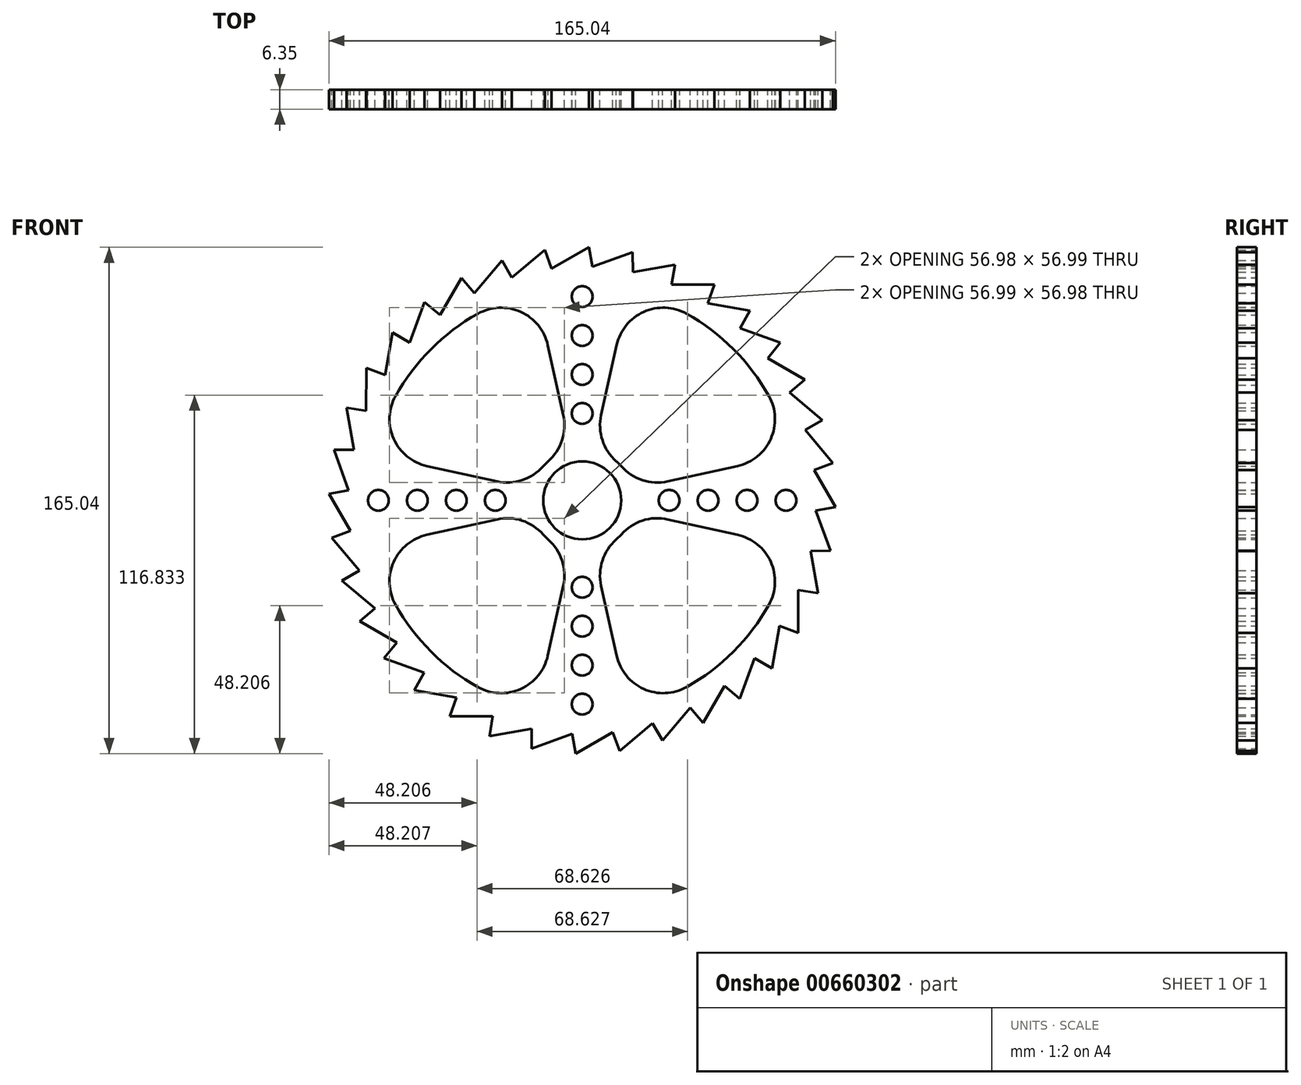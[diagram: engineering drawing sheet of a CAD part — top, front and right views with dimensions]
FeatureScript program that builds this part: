
annotation { "Feature Type Name" : "Feature", "Feature Type Description" : "" }
export const myFeature = defineFeature(function(context is Context, id is Id, definition is map)
    precondition{}
    {
        {
            var Q0;
            Q0=qCreatedBy(makeId("Front.planeOp"),FACE);
            var sketch = newSketch(context, id + "F0", { "sketchPlane" : qUnion([Q0])});
            skCircle(sketch, "E0", {"center": v(0, 0) * mm, "radius": 82.55 * mm, "construction": true});
            skCircle(sketch, "E1", {"center": v(0, 0) * mm, "radius": 76.2 * mm, "construction": true});
            skLineSegment(sketch, "E2", {"start": v(0, 0) * mm, "end": v(-97.62, 21.64) * mm, "construction": true});
            skLineSegment(sketch, "E3", {"start": v(0, 0) * mm, "end": v(-99.58, 4.35) * mm, "construction": true});
            skLineSegment(sketch, "E4", {"start": v(-76.13, 3.32) * mm, "end": v(-80.9, 16.46) * mm});
            skLineSegment(sketch, "E5", {"start": v(-80.9, 16.46) * mm, "end": v(-74.4, 16.5) * mm});
            skLineSegment(sketch, "E6.1.0", {"start": v(-82.52, 2.16) * mm, "end": v(-76.13, 3.32) * mm});
            skLineSegment(sketch, "E6.1.1", {"start": v(-75.55, -9.95) * mm, "end": v(-82.52, 2.16) * mm});
            skLineSegment(sketch, "E6.2.0", {"start": v(-81.64, -12.2) * mm, "end": v(-75.55, -9.95) * mm});
            skLineSegment(sketch, "E6.2.1", {"start": v(-72.67, -22.91) * mm, "end": v(-81.64, -12.2) * mm});
            skLineSegment(sketch, "E6.3.0", {"start": v(-78.28, -26.2) * mm, "end": v(-72.67, -22.91) * mm});
            skLineSegment(sketch, "E6.3.1", {"start": v(-67.6, -35.19) * mm, "end": v(-78.28, -26.2) * mm});
            skLineSegment(sketch, "E6.4.0", {"start": v(-72.55, -39.4) * mm, "end": v(-67.6, -35.19) * mm});
            skLineSegment(sketch, "E6.4.1", {"start": v(-60.45, -46.39) * mm, "end": v(-72.55, -39.4) * mm});
            skLineSegment(sketch, "E6.5.0", {"start": v(-64.6, -51.4) * mm, "end": v(-60.45, -46.39) * mm});
            skLineSegment(sketch, "E6.5.1", {"start": v(-51.48, -56.18) * mm, "end": v(-64.6, -51.4) * mm});
            skLineSegment(sketch, "E6.6.0", {"start": v(-54.7, -61.83) * mm, "end": v(-51.48, -56.18) * mm});
            skLineSegment(sketch, "E6.6.1", {"start": v(-40.94, -64.27) * mm, "end": v(-54.7, -61.83) * mm});
            skLineSegment(sketch, "E6.7.0", {"start": v(-43.13, -70.39) * mm, "end": v(-40.94, -64.27) * mm});
            skLineSegment(sketch, "E6.7.1", {"start": v(-29.16, -70.4) * mm, "end": v(-43.13, -70.39) * mm});
            skLineSegment(sketch, "E6.8.0", {"start": v(-30.25, -76.8) * mm, "end": v(-29.16, -70.4) * mm});
            skLineSegment(sketch, "E6.8.1", {"start": v(-16.5, -74.4) * mm, "end": v(-30.25, -76.8) * mm});
            skLineSegment(sketch, "E6.9.0", {"start": v(-16.46, -80.9) * mm, "end": v(-16.5, -74.4) * mm});
            skLineSegment(sketch, "E6.9.1", {"start": v(-3.32, -76.13) * mm, "end": v(-16.46, -80.9) * mm});
            skLineSegment(sketch, "E6.10.0", {"start": v(-2.16, -82.52) * mm, "end": v(-3.32, -76.13) * mm});
            skLineSegment(sketch, "E6.10.1", {"start": v(9.95, -75.55) * mm, "end": v(-2.16, -82.52) * mm});
            skLineSegment(sketch, "E6.11.0", {"start": v(12.2, -81.64) * mm, "end": v(9.95, -75.55) * mm});
            skLineSegment(sketch, "E6.11.1", {"start": v(22.91, -72.67) * mm, "end": v(12.2, -81.64) * mm});
            skLineSegment(sketch, "E6.12.0", {"start": v(26.2, -78.28) * mm, "end": v(22.91, -72.67) * mm});
            skLineSegment(sketch, "E6.12.1", {"start": v(35.19, -67.6) * mm, "end": v(26.2, -78.28) * mm});
            skLineSegment(sketch, "E6.13.0", {"start": v(39.4, -72.55) * mm, "end": v(35.19, -67.6) * mm});
            skLineSegment(sketch, "E6.13.1", {"start": v(46.39, -60.45) * mm, "end": v(39.4, -72.55) * mm});
            skLineSegment(sketch, "E6.14.0", {"start": v(51.4, -64.6) * mm, "end": v(46.39, -60.45) * mm});
            skLineSegment(sketch, "E6.14.1", {"start": v(56.18, -51.48) * mm, "end": v(51.4, -64.6) * mm});
            skLineSegment(sketch, "E6.15.0", {"start": v(61.83, -54.7) * mm, "end": v(56.18, -51.48) * mm});
            skLineSegment(sketch, "E6.15.1", {"start": v(64.27, -40.94) * mm, "end": v(61.83, -54.7) * mm});
            skLineSegment(sketch, "E6.16.0", {"start": v(70.39, -43.13) * mm, "end": v(64.27, -40.94) * mm});
            skLineSegment(sketch, "E6.16.1", {"start": v(70.4, -29.16) * mm, "end": v(70.39, -43.13) * mm});
            skLineSegment(sketch, "E6.17.0", {"start": v(76.8, -30.25) * mm, "end": v(70.4, -29.16) * mm});
            skLineSegment(sketch, "E6.17.1", {"start": v(74.4, -16.5) * mm, "end": v(76.8, -30.25) * mm});
            skLineSegment(sketch, "E6.18.0", {"start": v(80.9, -16.46) * mm, "end": v(74.4, -16.5) * mm});
            skLineSegment(sketch, "E6.18.1", {"start": v(76.13, -3.32) * mm, "end": v(80.9, -16.46) * mm});
            skLineSegment(sketch, "E6.19.0", {"start": v(82.52, -2.16) * mm, "end": v(76.13, -3.32) * mm});
            skLineSegment(sketch, "E6.19.1", {"start": v(75.55, 9.95) * mm, "end": v(82.52, -2.16) * mm});
            skLineSegment(sketch, "E6.20.0", {"start": v(81.64, 12.2) * mm, "end": v(75.55, 9.95) * mm});
            skLineSegment(sketch, "E6.20.1", {"start": v(72.67, 22.91) * mm, "end": v(81.64, 12.2) * mm});
            skLineSegment(sketch, "E6.21.0", {"start": v(78.28, 26.2) * mm, "end": v(72.67, 22.91) * mm});
            skLineSegment(sketch, "E6.21.1", {"start": v(67.6, 35.19) * mm, "end": v(78.28, 26.2) * mm});
            skLineSegment(sketch, "E6.22.0", {"start": v(72.55, 39.4) * mm, "end": v(67.6, 35.19) * mm});
            skLineSegment(sketch, "E6.22.1", {"start": v(60.45, 46.39) * mm, "end": v(72.55, 39.4) * mm});
            skLineSegment(sketch, "E6.23.0", {"start": v(64.6, 51.4) * mm, "end": v(60.45, 46.39) * mm});
            skLineSegment(sketch, "E6.23.1", {"start": v(51.48, 56.18) * mm, "end": v(64.6, 51.4) * mm});
            skLineSegment(sketch, "E6.24.0", {"start": v(54.7, 61.83) * mm, "end": v(51.48, 56.18) * mm});
            skLineSegment(sketch, "E6.24.1", {"start": v(40.94, 64.27) * mm, "end": v(54.7, 61.83) * mm});
            skLineSegment(sketch, "E6.25.0", {"start": v(43.13, 70.39) * mm, "end": v(40.94, 64.27) * mm});
            skLineSegment(sketch, "E6.25.1", {"start": v(29.16, 70.4) * mm, "end": v(43.13, 70.39) * mm});
            skLineSegment(sketch, "E6.26.0", {"start": v(30.25, 76.8) * mm, "end": v(29.16, 70.4) * mm});
            skLineSegment(sketch, "E6.26.1", {"start": v(16.5, 74.4) * mm, "end": v(30.25, 76.8) * mm});
            skLineSegment(sketch, "E6.27.0", {"start": v(16.46, 80.9) * mm, "end": v(16.5, 74.4) * mm});
            skLineSegment(sketch, "E6.27.1", {"start": v(3.32, 76.13) * mm, "end": v(16.46, 80.9) * mm});
            skLineSegment(sketch, "E6.28.0", {"start": v(2.16, 82.52) * mm, "end": v(3.32, 76.13) * mm});
            skLineSegment(sketch, "E6.28.1", {"start": v(-9.95, 75.55) * mm, "end": v(2.16, 82.52) * mm});
            skLineSegment(sketch, "E6.29.0", {"start": v(-12.2, 81.64) * mm, "end": v(-9.95, 75.55) * mm});
            skLineSegment(sketch, "E6.29.1", {"start": v(-22.91, 72.67) * mm, "end": v(-12.2, 81.64) * mm});
            skLineSegment(sketch, "E6.30.0", {"start": v(-26.2, 78.28) * mm, "end": v(-22.91, 72.67) * mm});
            skLineSegment(sketch, "E6.30.1", {"start": v(-35.19, 67.6) * mm, "end": v(-26.2, 78.28) * mm});
            skLineSegment(sketch, "E6.31.0", {"start": v(-39.4, 72.55) * mm, "end": v(-35.19, 67.6) * mm});
            skLineSegment(sketch, "E6.31.1", {"start": v(-46.39, 60.45) * mm, "end": v(-39.4, 72.55) * mm});
            skLineSegment(sketch, "E6.32.0", {"start": v(-51.4, 64.6) * mm, "end": v(-46.39, 60.45) * mm});
            skLineSegment(sketch, "E6.32.1", {"start": v(-56.18, 51.48) * mm, "end": v(-51.4, 64.6) * mm});
            skLineSegment(sketch, "E6.33.0", {"start": v(-61.83, 54.7) * mm, "end": v(-56.18, 51.48) * mm});
            skLineSegment(sketch, "E6.33.1", {"start": v(-64.27, 40.94) * mm, "end": v(-61.83, 54.7) * mm});
            skLineSegment(sketch, "E6.34.0", {"start": v(-70.39, 43.13) * mm, "end": v(-64.27, 40.94) * mm});
            skLineSegment(sketch, "E6.34.1", {"start": v(-70.4, 29.16) * mm, "end": v(-70.39, 43.13) * mm});
            skLineSegment(sketch, "E6.35.0", {"start": v(-76.8, 30.25) * mm, "end": v(-70.4, 29.16) * mm});
            skLineSegment(sketch, "E6.35.1", {"start": v(-74.4, 16.5) * mm, "end": v(-76.8, 30.25) * mm});
            skCircle(sketch, "E7", {"center": v(0, 0) * mm, "radius": 16.92 * mm, "construction": true});
            skLineSegment(sketch, "E8", {"start": v(0, 0) * mm, "end": v(97.72, 0) * mm, "construction": true});
            skLineSegment(sketch, "E9", {"start": v(27.83, 6.17) * mm, "end": v(50.62, 11.22) * mm});
            skLineSegment(sketch, "E10", {"start": v(0, 0) * mm, "end": v(0, 86.25) * mm, "construction": true});
            skArc(sketch, "E11", {"start": v(34.02, 60.84) * mm, "mid": v(49.3, 49.3) * mm, "end": v(60.84, 34.02) * mm});
            skLineSegment(sketch, "E12", {"start": v(6.17, 27.83) * mm, "end": v(11.22, 50.62) * mm});
            skPoint(sketch, "E13.visualSharp", {"position": v(15.09, 68.06) * mm});
            skArc(sketch, "E13.filletArc", {"start": v(34.02, 60.84) * mm, "mid": v(20.06, 61.46) * mm, "end": v(11.22, 50.62) * mm});
            skPoint(sketch, "E14.visualSharp", {"position": v(68.06, 15.09) * mm});
            skArc(sketch, "E14.filletArc", {"start": v(50.62, 11.22) * mm, "mid": v(61.46, 20.06) * mm, "end": v(60.84, 34.02) * mm});
            skArc(sketch, "E15", {"start": v(11.13, 12.74) * mm, "mid": v(11.96, 11.96) * mm, "end": v(12.74, 11.13) * mm});
            skPoint(sketch, "E16.visualSharp", {"position": v(3.66, 16.51) * mm});
            skArc(sketch, "E16.filletArc", {"start": v(6.17, 27.83) * mm, "mid": v(6.58, 19.6) * mm, "end": v(11.13, 12.74) * mm});
            skPoint(sketch, "E17.visualSharp", {"position": v(16.51, 3.66) * mm});
            skArc(sketch, "E17.filletArc", {"start": v(12.74, 11.13) * mm, "mid": v(19.6, 6.58) * mm, "end": v(27.83, 6.17) * mm});
            skLineSegment(sketch, "E18.1.0", {"start": v(-27.83, 6.17) * mm, "end": v(-50.62, 11.22) * mm});
            skArc(sketch, "E18.1.1", {"start": v(-60.84, 34.02) * mm, "mid": v(-61.46, 20.06) * mm, "end": v(-50.62, 11.22) * mm});
            skArc(sketch, "E18.1.2", {"start": v(-60.84, 34.02) * mm, "mid": v(-49.3, 49.3) * mm, "end": v(-34.02, 60.84) * mm});
            skArc(sketch, "E18.1.3", {"start": v(-11.22, 50.62) * mm, "mid": v(-20.06, 61.46) * mm, "end": v(-34.02, 60.84) * mm});
            skLineSegment(sketch, "E18.1.4", {"start": v(-6.17, 27.83) * mm, "end": v(-11.22, 50.62) * mm});
            skArc(sketch, "E18.1.5", {"start": v(-11.13, 12.74) * mm, "mid": v(-6.58, 19.6) * mm, "end": v(-6.17, 27.83) * mm});
            skArc(sketch, "E18.1.6", {"start": v(-27.83, 6.17) * mm, "mid": v(-19.6, 6.58) * mm, "end": v(-12.74, 11.13) * mm});
            skLineSegment(sketch, "E18.2.0", {"start": v(-6.17, -27.83) * mm, "end": v(-11.22, -50.62) * mm});
            skArc(sketch, "E18.2.1", {"start": v(-34.02, -60.84) * mm, "mid": v(-20.06, -61.46) * mm, "end": v(-11.22, -50.62) * mm});
            skArc(sketch, "E18.2.2", {"start": v(-34.02, -60.84) * mm, "mid": v(-49.3, -49.3) * mm, "end": v(-60.84, -34.02) * mm});
            skArc(sketch, "E18.2.3", {"start": v(-50.62, -11.22) * mm, "mid": v(-61.46, -20.06) * mm, "end": v(-60.84, -34.02) * mm});
            skLineSegment(sketch, "E18.2.4", {"start": v(-27.83, -6.17) * mm, "end": v(-50.62, -11.22) * mm});
            skArc(sketch, "E18.2.5", {"start": v(-12.74, -11.13) * mm, "mid": v(-19.6, -6.58) * mm, "end": v(-27.83, -6.17) * mm});
            skArc(sketch, "E18.2.6", {"start": v(-6.17, -27.83) * mm, "mid": v(-6.58, -19.6) * mm, "end": v(-11.13, -12.74) * mm});
            skLineSegment(sketch, "E18.3.0", {"start": v(27.83, -6.17) * mm, "end": v(50.62, -11.22) * mm});
            skArc(sketch, "E18.3.1", {"start": v(60.84, -34.02) * mm, "mid": v(61.46, -20.06) * mm, "end": v(50.62, -11.22) * mm});
            skArc(sketch, "E18.3.2", {"start": v(60.84, -34.02) * mm, "mid": v(49.3, -49.3) * mm, "end": v(34.02, -60.84) * mm});
            skArc(sketch, "E18.3.3", {"start": v(11.22, -50.62) * mm, "mid": v(20.06, -61.46) * mm, "end": v(34.02, -60.84) * mm});
            skLineSegment(sketch, "E18.3.4", {"start": v(6.17, -27.83) * mm, "end": v(11.22, -50.62) * mm});
            skArc(sketch, "E18.3.5", {"start": v(11.13, -12.74) * mm, "mid": v(6.58, -19.6) * mm, "end": v(6.17, -27.83) * mm});
            skArc(sketch, "E18.3.6", {"start": v(27.83, -6.17) * mm, "mid": v(19.6, -6.58) * mm, "end": v(12.74, -11.13) * mm});
            skCircle(sketch, "E19", {"center": v(0, 0) * mm, "radius": 12.7 * mm});
            skCircle(sketch, "E20", {"center": v(28.33, 0) * mm, "radius": 3.4 * mm});
            skCircle(sketch, "E21.1.0.0", {"center": v(41.03, 0) * mm, "radius": 3.4 * mm});
            skCircle(sketch, "E21.2.0.0", {"center": v(53.73, 0) * mm, "radius": 3.4 * mm});
            skCircle(sketch, "E21.3.0.0", {"center": v(66.43, 0) * mm, "radius": 3.4 * mm});
            skLineSegment(sketch, "E21.direction1", {"start": v(28.33, 0) * mm, "end": v(41.03, 0) * mm, "construction": true});
            skCircle(sketch, "E22.1.0", {"center": v(0, 28.33) * mm, "radius": 3.4 * mm});
            skCircle(sketch, "E22.1.1", {"center": v(0, 41.03) * mm, "radius": 3.4 * mm});
            skCircle(sketch, "E22.1.2", {"center": v(0, 53.73) * mm, "radius": 3.4 * mm});
            skCircle(sketch, "E22.1.3", {"center": v(0, 66.43) * mm, "radius": 3.4 * mm});
            skCircle(sketch, "E22.2.0", {"center": v(-28.33, 0) * mm, "radius": 3.4 * mm});
            skCircle(sketch, "E22.2.1", {"center": v(-41.03, 0) * mm, "radius": 3.4 * mm});
            skCircle(sketch, "E22.2.2", {"center": v(-53.73, 0) * mm, "radius": 3.4 * mm});
            skCircle(sketch, "E22.2.3", {"center": v(-66.43, 0) * mm, "radius": 3.4 * mm});
            skCircle(sketch, "E22.3.0", {"center": v(0, -28.33) * mm, "radius": 3.4 * mm});
            skCircle(sketch, "E22.3.1", {"center": v(0, -41.03) * mm, "radius": 3.4 * mm});
            skCircle(sketch, "E22.3.2", {"center": v(0, -53.73) * mm, "radius": 3.4 * mm});
            skCircle(sketch, "E22.3.3", {"center": v(0, -66.43) * mm, "radius": 3.4 * mm});
            skLineSegment(sketch, "E23", {"start": v(-12.74, 11.13) * mm, "end": v(-11.13, 12.74) * mm});
            skLineSegment(sketch, "E24", {"start": v(-12.74, -11.13) * mm, "end": v(-11.13, -12.74) * mm});
            skLineSegment(sketch, "E25", {"start": v(11.13, -12.74) * mm, "end": v(12.74, -11.13) * mm});
            skSolve(sketch);
        }
        {
            var Q0;
            Q0 = qSketchRegion(id + "F0", true);
            extrude(context, id + "F1", {"entities" : qUnion([Q0]), "depth" : 6.35 * mm, "offsetDistance" : 25.4 * mm});
        }
    });
